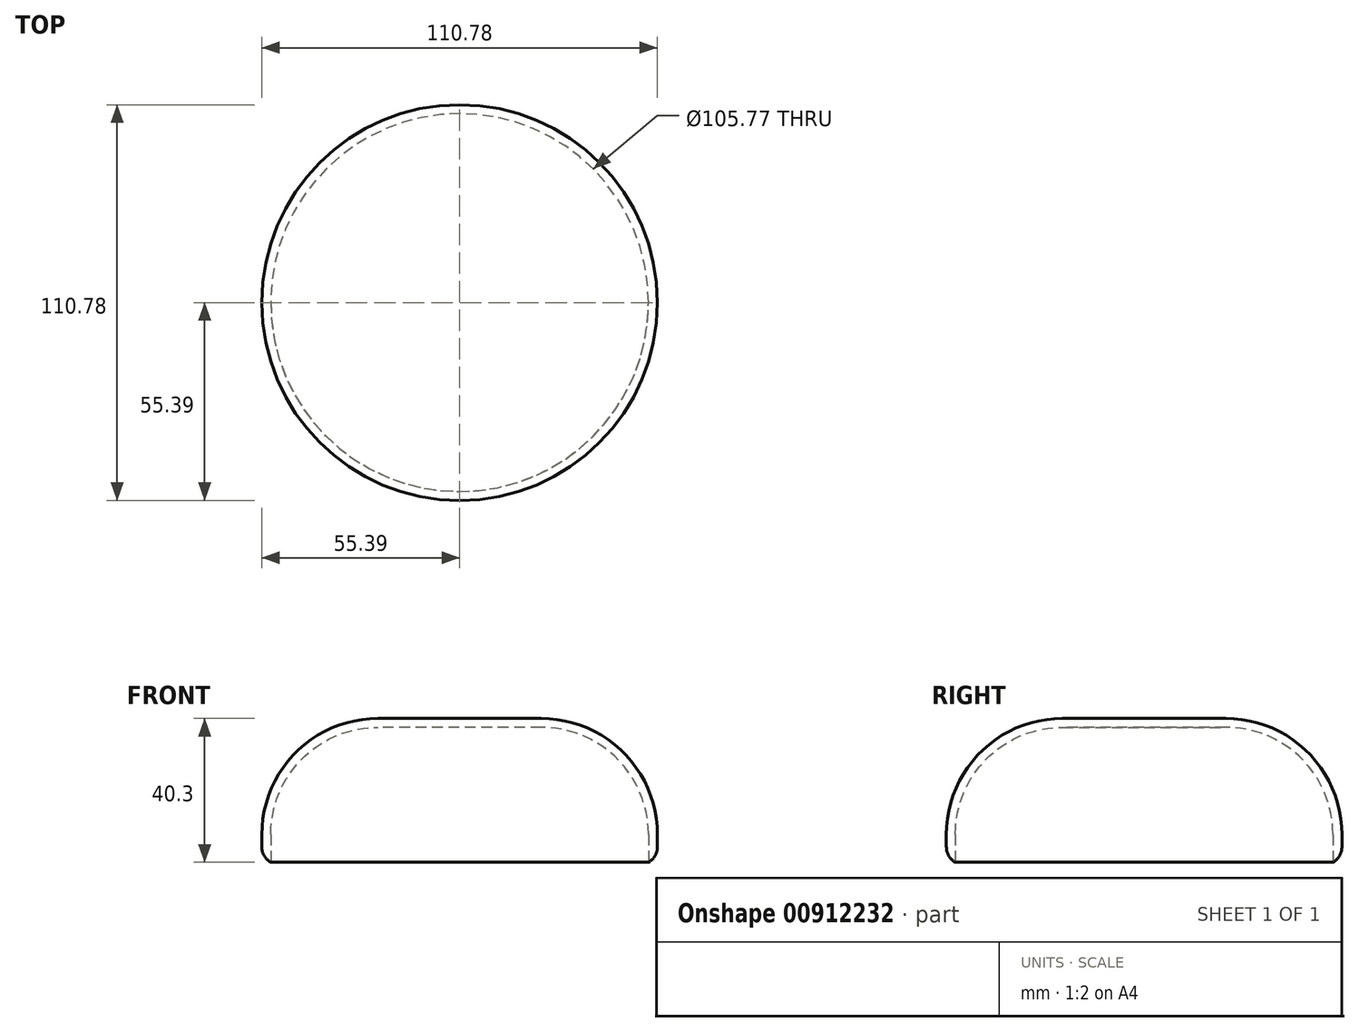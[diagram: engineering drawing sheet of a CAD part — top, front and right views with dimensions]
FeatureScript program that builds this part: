
annotation { "Feature Type Name" : "Feature", "Feature Type Description" : "" }
export const myFeature = defineFeature(function(context is Context, id is Id, definition is map)
    precondition{}
    {
        {
            var Q0;
            Q0=qCreatedBy(makeId("Top.planeOp"),FACE);
            var sketch = newSketch(context, id + "F0", { "sketchPlane" : qUnion([Q0])});
            skCircle(sketch, "E0", {"center": v(0, 0) * mm, "radius": 52.89 * mm});
            skLineSegment(sketch, "E1", {"start": v(0, 0) * mm, "end": v(0, 52.89) * mm});
            skLineSegment(sketch, "E2", {"start": v(0, 0) * mm, "end": v(0, -52.89) * mm});
            skLineSegment(sketch, "E3", {"start": v(0, 0) * mm, "end": v(52.89, 0) * mm});
            skLineSegment(sketch, "E4", {"start": v(0, 0) * mm, "end": v(-52.89, 0) * mm});
            skSolve(sketch);
        }
        {
            var Q0;
            Q0 = qSketchRegion(id + "F0", true);
            var Q1;
            Q1=makeQuery(id+"F0.imprint","IMPRINT",FACE,{"disambiguationData":[TD([[makeQuery(id+"F0.imprint","IMPRINT",EDGE,{"derivedFrom":sQuery(id+"F0.wireOp",EDGE,"E0")}),1.0]])]});
            extrude(context, id + "F1", {"entities" : qUnion([Q0, Q1]), "depth" : 37.8 * mm, "offsetDistance" : 25 * mm});
        }
        {
            var Q0;
            Q0=makeQuery(id+"F1.opExtrude","CAP_EDGE",EDGE,{"disambiguationData":[OSD([sQuery(id+"F0.wireOp",EDGE,"E0")])],"isStart":false});
            fillet(context, id + "F2", {"entities" : qUnion([Q0]), "radius" : 30 * mm, "tangentPropagation" : true, "allowEdgeOverflow" : false});
        }
        {
            var Q0;
            Q0=makeQuery(id+"F1.opExtrude","CAP_FACE",FACE,{"disambiguationData":[OSD([sQuery(id+"F0.wireOp",EDGE,"E0")])],"isStart":true});
            shell(context, id + "F3", {"entities" : qUnion([Q0]), "thickness" : 2.5 * mm, "oppositeDirection" : true});
        }
        {
            var Q0;
            Q0=makeQuery(id+"F1.opExtrude","CAP_EDGE",EDGE,{"disambiguationData":[OSD([sQuery(id+"F0.wireOp",EDGE,"E0")])],"isStart":true});
            fillet(context, id + "F4", {"entities" : qUnion([Q0]), "radius" : 5 * mm, "tangentPropagation" : true, "allowEdgeOverflow" : false});
        }
    });
